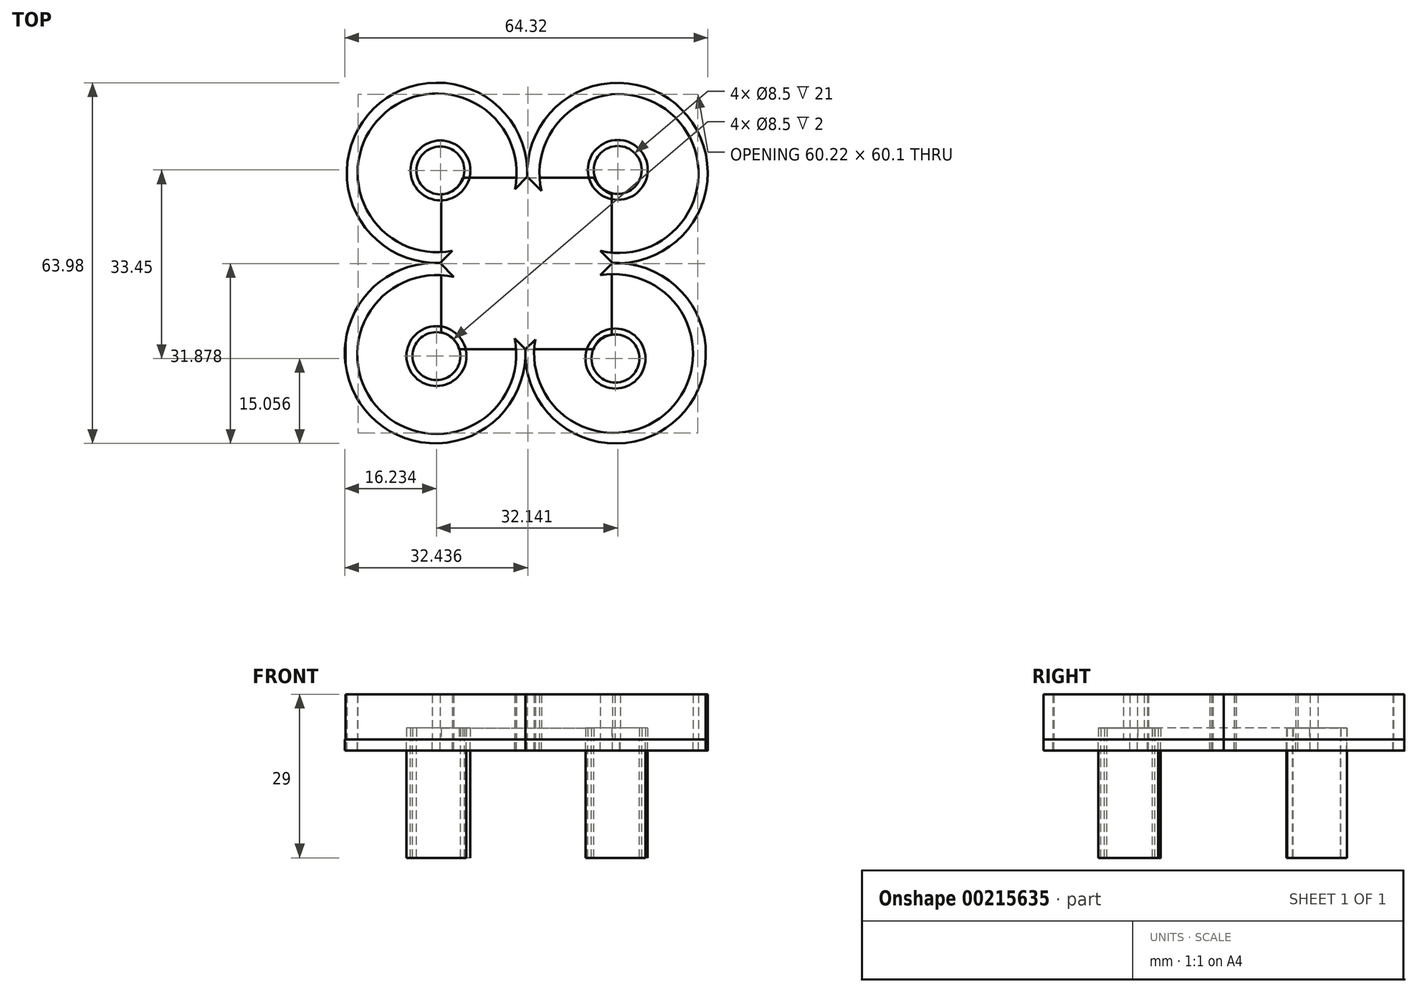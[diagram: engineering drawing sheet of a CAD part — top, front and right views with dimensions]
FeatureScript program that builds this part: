
annotation { "Feature Type Name" : "Feature", "Feature Type Description" : "" }
export const myFeature = defineFeature(function(context is Context, id is Id, definition is map)
    precondition{}
    {
        {
            var Q0;
            Q0=qCreatedBy(makeId("Top.planeOp"),FACE);
            var sketch = newSketch(context, id + "F0", { "sketchPlane" : qUnion([Q0])});
            skLineSegment(sketch, "E0", {"start": v(-44.03, -13.47) * mm, "end": v(-44.03, -17.15) * mm});
            skArc(sketch, "E1", {"start": v(-11.8, 15.97) * mm, "mid": v(-39.04, 28.04) * mm, "end": v(-27.28, 0.67) * mm});
            skArc(sketch, "E2", {"start": v(-27.28, 0.67) * mm, "mid": v(-39.52, -26.55) * mm, "end": v(-12.15, -14.63) * mm});
            skArc(sketch, "E3", {"start": v(3.32, 0.67) * mm, "mid": v(15.56, 27.9) * mm, "end": v(-11.8, 15.97) * mm});
            skArc(sketch, "E4", {"start": v(4.54, 0.65) * mm, "mid": v(3.9, 0.67) * mm, "end": v(3.25, 0.67) * mm});
            skPoint(sketch, "E5", {"position": v(-28.65, 0.69) * mm});
            skPoint(sketch, "E6", {"position": v(-11.8, 15.97) * mm});
            skArc(sketch, "E7", {"start": v(-12.15, -14.63) * mm, "mid": v(15.08, -26.7) * mm, "end": v(3.32, 0.67) * mm});
            skPoint(sketch, "E8", {"position": v(3.32, 0.67) * mm});
            skPoint(sketch, "E9", {"position": v(-12.15, -14.63) * mm});
            skLineSegment(sketch, "E10", {"start": v(-27.28, 0.67) * mm, "end": v(-11.8, 15.97) * mm});
            skLineSegment(sketch, "E11", {"start": v(3.32, 0.67) * mm, "end": v(-12.15, -14.63) * mm});
            skLineSegment(sketch, "E12", {"start": v(-27.28, 0.67) * mm, "end": v(-12.15, -14.63) * mm});
            skLineSegment(sketch, "E13", {"start": v(3.32, 0.67) * mm, "end": v(-11.8, 15.97) * mm});
            skCircle(sketch, "E14", {"center": v(-27.8, 16.66) * mm, "radius": 14.09 * mm});
            skCircle(sketch, "E15", {"center": v(-27.86, -15.56) * mm, "radius": 14.09 * mm});
            skCircle(sketch, "E16", {"center": v(4.44, 16.55) * mm, "radius": 14.09 * mm});
            skCircle(sketch, "E17", {"center": v(3.49, -15.37) * mm, "radius": 14.09 * mm});
            skSolve(sketch);
        }
        {
            var Q0;
            {var subQ1=sQuery(id+"F0.wireOp",EDGE,"E3");var subQ2=sQuery(id+"F0.wireOp",EDGE,"E1");var subQ4=makeQuery(id+"F0.imprint","INTERSECT",VERTEX,{"derivedFrom":[subQ2,subQ1]});Q0=makeQuery(id+"F0.imprint","IMPRINT",FACE,{"disambiguationData":[TD([[makeQuery(id+"F0.imprint","IMPRINT",EDGE,{"disambiguationData":[TD([[subQ4,-1.0]])],"derivedFrom":subQ2}),1.0]])]});}
            var Q1;
            {var subQ1=sQuery(id+"F0.wireOp",EDGE,"E0");Q1=makeQuery(id+"F0.imprint","IMPRINT",FACE,{"disambiguationData":[TD([[makeQuery(id+"F0.imprint","IMPRINT",EDGE,{"derivedFrom":subQ1}),1.0]])]});}
            var Q2;
            {var subQ5=sQuery(id+"F0.wireOp",EDGE,"E3");var subQ6=sQuery(id+"F0.wireOp",EDGE,"E1");var subQ7=makeQuery(id+"F0.imprint","INTERSECT",VERTEX,{"derivedFrom":[subQ6,subQ5]});Q2=makeQuery(id+"F0.imprint","IMPRINT",FACE,{"disambiguationData":[TD([[makeQuery(id+"F0.imprint","IMPRINT",EDGE,{"disambiguationData":[TD([[subQ7,1.0]])],"derivedFrom":subQ5}),1.0]])]});}
            var Q3;
            {var subQ3=sQuery(id+"F0.wireOp",EDGE,"E3");var subQ5=makeQuery(id+"F0.imprint","INTERSECT",VERTEX,{"derivedFrom":[subQ3,sQuery(id+"F0.wireOp",EDGE,"E4")]});Q3=makeQuery(id+"F0.imprint","IMPRINT",FACE,{"disambiguationData":[TD([[makeQuery(id+"F0.imprint","IMPRINT",EDGE,{"disambiguationData":[TD([[subQ5,-1.0]])],"derivedFrom":subQ3}),-1.0]])]});}
            extrude(context, id + "F1", {"entities" : qUnion([Q0, Q1, Q2, Q3]), "depth" : 8 * mm});
        }
        {
            var Q0;
            Q0=qCreatedBy(makeId("Top.planeOp"),FACE);
            var sketch = newSketch(context, id + "F2", { "sketchPlane" : qUnion([Q0])});
            skCircle(sketch, "E18", {"center": v(-27.2, 17.1) * mm, "radius": 4.25 * mm});
            skCircle(sketch, "E19", {"center": v(-27.2, 17.1) * mm, "radius": 5.3 * mm});
            skCircle(sketch, "E20", {"center": v(4.23, 17.19) * mm, "radius": 4.25 * mm});
            skCircle(sketch, "E21", {"center": v(4.23, 17.19) * mm, "radius": 5.3 * mm});
            skCircle(sketch, "E22", {"center": v(-27.9, -15.83) * mm, "radius": 4.25 * mm});
            skCircle(sketch, "E23", {"center": v(-27.9, -15.83) * mm, "radius": 5.3 * mm});
            skCircle(sketch, "E24", {"center": v(3.82, -16.26) * mm, "radius": 4.25 * mm});
            skCircle(sketch, "E25", {"center": v(3.82, -16.26) * mm, "radius": 5.3 * mm});
            skSolve(sketch);
        }
        {
            var Q0;
            Q0=makeQuery(id+"F2.imprint","IMPRINT",FACE,{"disambiguationData":[TD([[makeQuery(id+"F2.imprint","IMPRINT",EDGE,{"derivedFrom":sQuery(id+"F2.wireOp",EDGE,"E18")}),-1.0]])]});
            var Q1;
            Q1=makeQuery(id+"F2.imprint","IMPRINT",FACE,{"disambiguationData":[TD([[makeQuery(id+"F2.imprint","IMPRINT",EDGE,{"derivedFrom":sQuery(id+"F2.wireOp",EDGE,"E20")}),-1.0]])]});
            var Q2;
            Q2=makeQuery(id+"F2.imprint","IMPRINT",FACE,{"disambiguationData":[TD([[makeQuery(id+"F2.imprint","IMPRINT",EDGE,{"derivedFrom":sQuery(id+"F2.wireOp",EDGE,"E22")}),-1.0]])]});
            var Q3;
            Q3=makeQuery(id+"F2.imprint","IMPRINT",FACE,{"disambiguationData":[TD([[makeQuery(id+"F2.imprint","IMPRINT",EDGE,{"derivedFrom":sQuery(id+"F2.wireOp",EDGE,"E24")}),-1.0]])]});
            extrude(context, id + "F3", {"entities" : qUnion([Q0, Q1, Q2, Q3]), "oppositeDirection" : true, "depth" : 21 * mm});
        }
        {
            var Q0;
            Q0 = qSketchRegion(id + "F2", true);
            extrude(context, id + "F4", {"entities" : qUnion([Q0]), "depth" : 2 * mm});
        }
        {
            var Q0;
            Q0 = qSketchRegion(id + "F0", true);
            extrude(context, id + "F5", {"entities" : qUnion([Q0]), "oppositeDirection" : true, "depth" : 2 * mm});
        }
        {
            var Q0;
            Q0=qCreatedBy(makeId("Top.planeOp"),FACE);
            var sketch = newSketch(context, id + "F6", { "sketchPlane" : qUnion([Q0])});
            skLineSegment(sketch, "E26.bottom", {"start": v(-23.24, 15.82) * mm, "end": v(0, 15.82) * mm});
            skLineSegment(sketch, "E26.top", {"start": v(-23.9, -14.58) * mm, "end": v(0, -14.58) * mm});
            skLineSegment(sketch, "E26.left", {"start": v(-27.03, 12.87) * mm, "end": v(-27.03, -11.63) * mm});
            skLineSegment(sketch, "E26.right", {"start": v(3.2, 12.87) * mm, "end": v(3.2, -12.06) * mm});
            skPoint(sketch, "E27", {"position": v(-27.03, 12.87) * mm});
            skPoint(sketch, "E28", {"position": v(-23.24, 15.82) * mm});
            skPoint(sketch, "E29", {"position": v(0, 15.82) * mm});
            skPoint(sketch, "E30", {"position": v(3.2, 12.87) * mm});
            skPoint(sketch, "E31", {"position": v(3.2, -12.06) * mm});
            skPoint(sketch, "E32", {"position": v(0, -14.58) * mm});
            skPoint(sketch, "E33", {"position": v(-23.9, -14.58) * mm});
            skPoint(sketch, "E34", {"position": v(-27.03, -11.63) * mm});
            skArc(sketch, "E35", {"start": v(-27.03, 12.87) * mm, "mid": v(-24.68, 13.76) * mm, "end": v(-23.24, 15.82) * mm});
            skArc(sketch, "E36", {"start": v(-23.9, -14.58) * mm, "mid": v(-25.04, -12.66) * mm, "end": v(-27.03, -11.63) * mm});
            skArc(sketch, "E37", {"start": v(3.2, -12.06) * mm, "mid": v(1.17, -12.78) * mm, "end": v(0, -14.58) * mm});
            skArc(sketch, "E38", {"start": v(0, 15.82) * mm, "mid": v(1.29, 14.01) * mm, "end": v(3.2, 12.87) * mm});
            skSolve(sketch);
        }
        {
            var Q0;
            Q0 = qSketchRegion(id + "F6", true);
            extrude(context, id + "F7", {"entities" : qUnion([Q0]), "depth" : 2 * mm});
        }
    });
